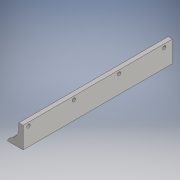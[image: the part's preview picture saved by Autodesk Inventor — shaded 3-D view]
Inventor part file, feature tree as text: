
AUTODESK INVENTOR PART (.ipt)
format: ipt  version: 2016 (Build 200138000, 138)  size: 107,008 bytes
history: native  units: in
note: dims shown in document units (in); Inventor stores cm internally (conversion verified against a paired STEP export)
features: extrude x1, hole x1, pattern_linear x1, sketch x1
ambient origin geometry x8: Origin, YZ Plane, XZ Plane, XY Plane, X Axis, Y Axis, Z Axis, Center Point
bodies: Solid1 (feature_tree)
feature tree (4):
  extrude  "Extrusion1"  Depth=1.0in
  hole  "Hole1"  [1 undecoded]
  pattern_linear  "Rectangular Pattern1"  Spacing1=7.0in  [1 undecoded]
  sketch  "Sketch1"  dims[d1=0.25in d7=1.0in d8=0.7282in d9=7.0in d10=0.0in d20=1.0in d21=1.0in d13=0.1575in d14=0.75in d15=0.375in d16=0.25in d17=0.5635in d18=1.0in d19=0.8108in d22=1.5748in d24=2.12in]
note: 2 required parameter values undecoded (feature->parameter linkage not recoverable at this tier; creation-order binding heuristic only, values carry confidence <= 0.55)
